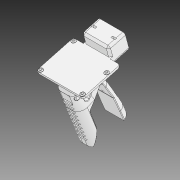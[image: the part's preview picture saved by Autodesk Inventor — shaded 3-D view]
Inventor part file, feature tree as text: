
AUTODESK INVENTOR PART (.ipt)
format: ipt  version: 2020 (Build 240168000, 168)  size: 2,263,040 bytes
history: native  units: in
note: dims shown in document units (in); Inventor stores cm internally (conversion verified against a paired STEP export)
features: sketch x23, extrude x22, fillet x7, projected_geometry x4, other x3, plane x3, chamfer x3, mirror x1, imported_body x1
ambient origin geometry x8: Origin, YZ Plane, XZ Plane, XY Plane, X Axis, Y Axis, Z Axis, Center Point
bodies: Solid1 (feature_tree)
feature tree (67):
  other  "Blocks"
  extrude  "Extrusion1"  Depth=0.1575in
  extrude  "Extrusion4"  Depth=0.3937in TaperAngle=0.0deg
  fillet  "Fillet1"  Radius=0.1378in
  extrude  "Extrusion5"  Depth=0.5906in
  extrude  "Extrusion6"  Depth=0.5906in TaperAngle=0.0deg
  plane  "Work Plane1"
  extrude  "Extrusion7"  Depth=0.2244in
  extrude  "Extrusion8"  Depth=0.2062in TaperAngle=0.0deg
  extrude  "Extrusion9"  Depth=0.3937in
  fillet  "Fillet2"  Radius=0.2062in
  chamfer  "Chamfer1"  Distance=0.2062in
  extrude  "Extrusion10"  TaperAngle=0.0deg  [1 undecoded]
  extrude  "Extrusion11"  Depth=0.3937in
  fillet  "Fillet3"  Radius=0.3937in
  extrude  "Extrusion12"  Depth=3.0907in TaperAngle=0.0deg
  fillet  "Fillet4"  Radius=1.4001in
  extrude  "Extrusion13"  Depth=0.1181in TaperAngle=0.0deg
  plane  "Work Plane2"
  extrude  "Extrusion15"  Depth=0.4724in
  extrude  "Extrusion16"  Depth=0.5906in
  mirror  "Mirror1"
  fillet  "Fillet5"  Radius=0.5906in
  extrude  "Extrusion17"  Depth=0.1181in
  extrude  "Extrusion18"  TaperAngle=0.0deg  [1 undecoded]
  fillet  "Fillet6"  Radius=0.3937in
  sketch  "Sketch21"  dims[d62=75.0deg d63=0.0in d64=0.0in d65=0.3937in d66=0.0in]
  extrude  "Extrusion19"  [1 undecoded]
  extrude  "Extrusion20"  Depth=0.2244in
  extrude  "Extrusion21"  Depth=0.5906in TaperAngle=0.0deg
  plane  "Work Plane3"
  extrude  "Extrusion22"  Depth=0.1181in TaperAngle=45.0deg
  extrude  "Extrusion23"  Depth=0.1181in
  chamfer  "Chamfer2"  Distance=0.1181in
  extrude  "Extrusion24"  Depth=0.0591in TaperAngle=0.0deg
  extrude  "Extrusion25"  Depth=0.1181in
  chamfer  "Chamfer3"  Distance=0.1181in
  fillet  "Fillet7"  [1 undecoded]
  sketch  "Sketch1"  dims[d0=0.0in d1=0.0in d2=0.1575in]
  sketch  "Sketch5"  dims[d7=3.3563in d8=0.0in d9=0.3937in d10=0.0in d11=0.1378in]
  sketch  "Sketch6"  dims[d12=1.1024in d13=0.5906in]
  sketch  "Sketch7"  dims[d14=0.4724in d15=0.5906in d16=0.0in]
  sketch  "Sketch8"  dims[d17=-0.3937in d18=0.2244in]
  sketch  "Sketch9"  dims[d19=0.1024in d20=0.0in d21=0.2062in d22=0.0in]
  sketch  "Sketch10"  dims[d23=0.3937in d24=0.0in d25=0.0787in]
  sketch  "Sketch11"  dims[d26=0.0276in d27=0.0787in d28=45.0deg d29=0.2062in d30=0.0in d31=0.2062in d32=0.0in]
  projected_geometry  "Projected Loop2"
  sketch  "Sketch12"  dims[d33=0.0315in d34=0.0in d35=0.0in]
  sketch  "Sketch13"  dims[d36=0.1969in d37=0.9687in d38=0.3937in]
  sketch  "Sketch14"  dims[d40=1.5in d41=0.0in d47=3.0907in d48=0.0in d49=1.4001in d50=0.0in]
  sketch  "Sketch17"  dims[d51=0.1181in d52=1.378in d53=0.0in]
  sketch  "Sketch18"  dims[d54=0.1378in d55=0.4724in]
  projected_geometry  "Projected Loop4"
  sketch  "Sketch19"  dims[d56=1.1024in d57=0.5906in d58=0.5906in d59=0.0in]
  sketch  "Sketch20"  dims[d60=0.1181in d61=0.1969in]
  projected_geometry  "Projected Loop6"
  sketch  "Sketch22"  dims[d67=0.3937in d68=0.0in d69=-0.3937in]
  sketch  "Sketch23"  dims[d70=0.2244in d71=0.2244in]
  sketch  "Sketch24"  dims[d72=0.1024in d73=0.0in d74=0.5906in d75=0.0in]
  projected_geometry  "Projected Loop7"
  sketch  "Sketch25"  dims[d76=0.9843in d77=0.1181in d78=0.0787in d79=45.0deg]
  sketch  "Sketch27"  dims[d80=2.3425in d81=2.6181in d82=2.1575in d83=1.9094in d84=0.6299in d85=0.1063in d86=0.0394in d87=0.1181in d88=0.0in]
  sketch  "Sketch28"  dims[d89=0.2362in d90=0.0591in d91=0.0in]
  other  "Block1"
  sketch  "Sketch29"  dims[d92=0.0394in d93=0.0787in d94=45.0deg d95=0.1181in d96=0.1181in]
  imported_body  "Base1"
  other  "Block1:1"
note: 4 required parameter values undecoded (feature->parameter linkage not recoverable at this tier; creation-order binding heuristic only, values carry confidence <= 0.55)
